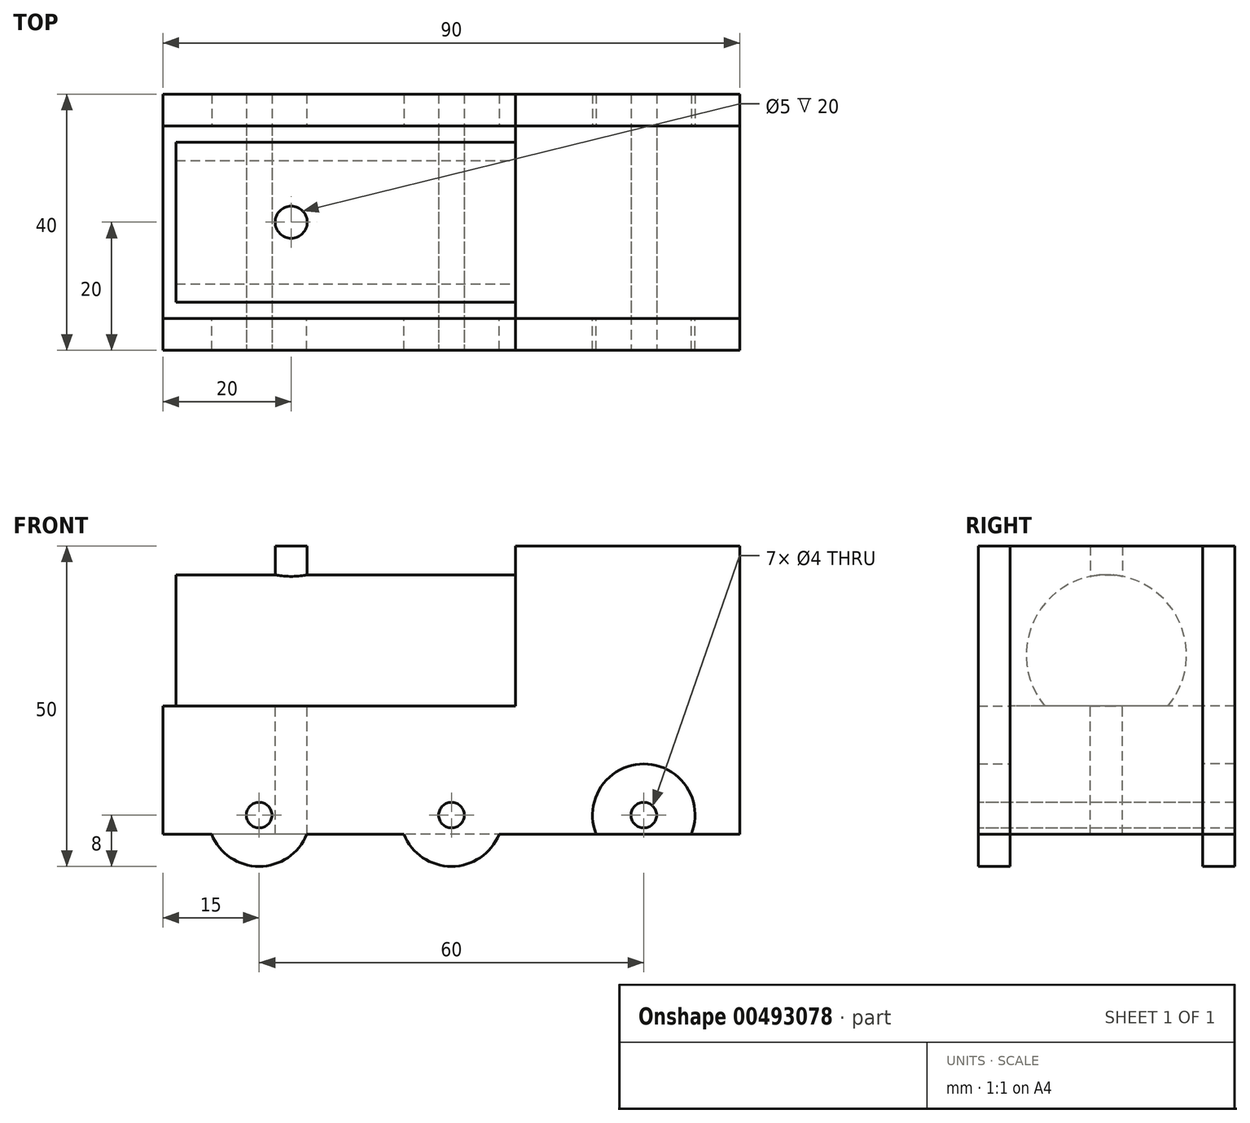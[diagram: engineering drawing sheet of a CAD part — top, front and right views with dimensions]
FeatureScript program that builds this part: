
annotation { "Feature Type Name" : "Feature", "Feature Type Description" : "" }
export const myFeature = defineFeature(function(context is Context, id is Id, definition is map)
    precondition{}
    {
        {
            var Q0;
            Q0=qCreatedBy(makeId("Top.planeOp"),FACE);
            var sketch = newSketch(context, id + "F0", { "sketchPlane" : qUnion([Q0])});
            skLineSegment(sketch, "E0.bottom", {"start": v(0, 0) * mm, "end": v(-90, 0) * mm});
            skLineSegment(sketch, "E0.top", {"start": v(0, -30) * mm, "end": v(-90, -30) * mm});
            skLineSegment(sketch, "E0.left", {"start": v(0, 0) * mm, "end": v(0, -30) * mm});
            skLineSegment(sketch, "E0.right", {"start": v(-90, 0) * mm, "end": v(-90, -30) * mm});
            skSolve(sketch);
        }
        {
            var Q0;
            Q0=makeQuery(id+"F0.imprint","IMPRINT",FACE,{"disambiguationData":[TD([[makeQuery(id+"F0.imprint","IMPRINT",EDGE,{"derivedFrom":sQuery(id+"F0.wireOp",EDGE,"E0.bottom")}),1.0]])]});
            extrude(context, id + "F1", {"entities" : qUnion([Q0]), "depth" : 20 * mm});
        }
        {
            var Q0;
            Q0=makeQuery(id+"F1.opExtrude","CAP_FACE",FACE,{"disambiguationData":[OSD([sQuery(id+"F0.wireOp",EDGE,"E0.bottom"),sQuery(id+"F0.wireOp",EDGE,"E0.top"),sQuery(id+"F0.wireOp",EDGE,"E0.left"),sQuery(id+"F0.wireOp",EDGE,"E0.right")])],"isStart":false});
            var sketch = newSketch(context, id + "F2", { "sketchPlane" : qUnion([Q0])});
            skLineSegment(sketch, "E1.bottom", {"start": v(0, 0) * mm, "end": v(-35, 0) * mm});
            skLineSegment(sketch, "E1.top", {"start": v(0, -30) * mm, "end": v(-35, -30) * mm});
            skLineSegment(sketch, "E1.left", {"start": v(0, 0) * mm, "end": v(0, -30) * mm});
            skLineSegment(sketch, "E1.right", {"start": v(-35, 0) * mm, "end": v(-35, -30) * mm});
            skSolve(sketch);
        }
        {
            var Q0;
            Q0 = qSketchRegion(id + "F2", true);
            extrude(context, id + "F3", {"entities" : qUnion([Q0]), "operationType" : NewBodyOperationType.ADD, "depth" : 25 * mm});
        }
        {
            var Q0;
            Q0=makeQuery(id+"F3.opExtrude","SWEPT_FACE",FACE,{"disambiguationData":[OSD([sQuery(id+"F2.wireOp",EDGE,"E1.right")])]});
            var sketch = newSketch(context, id + "F4", { "sketchPlane" : qUnion([Q0])});
            skArc(sketch, "E2", {"start": v(24.6, 20) * mm, "mid": v(15, 40.5) * mm, "end": v(5.4, 20) * mm});
            skPoint(sketch, "E2.centerSnap0", {"position": v(15, 20) * mm});
            skLineSegment(sketch, "E3", {"start": v(5.4, 20) * mm, "end": v(24.6, 20) * mm});
            skSolve(sketch);
        }
        {
            var Q0;
            Q0=makeQuery(id+"F4.imprint","IMPRINT",FACE,{"disambiguationData":[TD([[makeQuery(id+"F4.imprint","IMPRINT",EDGE,{"derivedFrom":sQuery(id+"F4.wireOp",EDGE,"E2")}),1.0]])]});
            extrude(context, id + "F5", {"entities" : qUnion([Q0]), "depth" : 53 * mm});
        }
        {
            var Q0;
            Q0=makeQuery(id+"F3.opExtrude","CAP_FACE",FACE,{"disambiguationData":[OSD([sQuery(id+"F2.wireOp",EDGE,"E1.bottom"),sQuery(id+"F2.wireOp",EDGE,"E1.top"),sQuery(id+"F2.wireOp",EDGE,"E1.left"),sQuery(id+"F2.wireOp",EDGE,"E1.right")])],"isStart":false});
            var sketch = newSketch(context, id + "F6", { "sketchPlane" : qUnion([Q0])});
            skLineSegment(sketch, "E4.0", {"start": v(-88, -27.5) * mm, "end": v(-88, -2.5) * mm});
            skLineSegment(sketch, "E5.0", {"start": v(-35, 0) * mm, "end": v(-35, -30) * mm});
            skLineSegment(sketch, "E6", {"start": v(-35, -15) * mm, "end": v(-88, -15) * mm, "construction": true});
            skCircle(sketch, "E7", {"center": v(-70, -15) * mm, "radius": 2.5 * mm});
            skSolve(sketch);
        }
        {
            var Q0;
            Q0=makeQuery(id+"F6.imprint","IMPRINT",FACE,{"disambiguationData":[TD([[makeQuery(id+"F6.imprint","IMPRINT",EDGE,{"derivedFrom":sQuery(id+"F6.wireOp",EDGE,"E7")}),1.0]])]});
            extrude(context, id + "F7", {"entities" : qUnion([Q0]), "operationType" : NewBodyOperationType.REMOVE, "oppositeDirection" : true, "depth" : 69.3 * mm});
        }
        {
            var Q0;
            Q0=makeQuery(id+"F1.opExtrude","CAP_FACE",FACE,{"disambiguationData":[OSD([sQuery(id+"F0.wireOp",EDGE,"E0.bottom"),sQuery(id+"F0.wireOp",EDGE,"E0.top"),sQuery(id+"F0.wireOp",EDGE,"E0.left"),sQuery(id+"F0.wireOp",EDGE,"E0.right")])],"isStart":false});
            var sketch = newSketch(context, id + "F8", { "sketchPlane" : qUnion([Q0])});
            skCircle(sketch, "E8.0", {"center": v(-70, -15) * mm, "radius": 2.5 * mm});
            skSolve(sketch);
        }
        {
            var Q0;
            Q0 = qSketchRegion(id + "F8", true);
            extrude(context, id + "F9", {"entities" : qUnion([Q0]), "operationType" : NewBodyOperationType.ADD, "depth" : 25 * mm});
        }
        {
            var Q0;
            Q0=makeQuery(id+"F3.boolean.opBoolean","MERGE",FACE,{"derivedFrom":[makeQuery(id+"F1.opExtrude","SWEPT_FACE",FACE,{"disambiguationData":[OSD([sQuery(id+"F0.wireOp",EDGE,"E0.top")])]}),makeQuery(id+"F3.opExtrude","SWEPT_FACE",FACE,{"disambiguationData":[OSD([sQuery(id+"F2.wireOp",EDGE,"E1.top")])]})]});
            var sketch = newSketch(context, id + "F10", { "sketchPlane" : qUnion([Q0])});
            skLineSegment(sketch, "E9", {"start": v(-90, 3) * mm, "end": v(0, 3) * mm, "construction": true});
            skCircle(sketch, "E10", {"center": v(-75, 3) * mm, "radius": 8 * mm});
            skCircle(sketch, "E11", {"center": v(-45, 3) * mm, "radius": 8 * mm});
            skCircle(sketch, "E12", {"center": v(-15, 3) * mm, "radius": 8 * mm});
            skSolve(sketch);
        }
        {
            var Q0;
            {var subQ0=sQuery(id+"F10.wireOp",EDGE,"E10");var subQ1=makeQuery(id+"F1.opExtrude","CAP_EDGE",EDGE,{"disambiguationData":[OSD([sQuery(id+"F0.wireOp",EDGE,"E0.top")])],"isStart":true});var subQ2=makeQuery(id+"F10.imprint","INTERSECT",VERTEX,{"disambiguationData":[OD(0.0)],"derivedFrom":[subQ1,subQ0]});Q0=makeQuery(id+"F10.imprint","IMPRINT",FACE,{"disambiguationData":[TD([[makeQuery(id+"F10.imprint","IMPRINT",EDGE,{"disambiguationData":[TD([[subQ2,1.0]])],"derivedFrom":subQ0}),1.0]])]});}
            var Q1;
            {var subQ0=sQuery(id+"F10.wireOp",EDGE,"E10");var subQ1=makeQuery(id+"F1.opExtrude","CAP_EDGE",EDGE,{"disambiguationData":[OSD([sQuery(id+"F0.wireOp",EDGE,"E0.top")])],"isStart":true});var subQ2=makeQuery(id+"F10.imprint","INTERSECT",VERTEX,{"disambiguationData":[OD(0.0)],"derivedFrom":[subQ1,subQ0]});Q1=makeQuery(id+"F10.imprint","IMPRINT",FACE,{"disambiguationData":[TD([[makeQuery(id+"F10.imprint","IMPRINT",EDGE,{"disambiguationData":[TD([[subQ2,-1.0]])],"derivedFrom":subQ0}),1.0]])]});}
            var Q2;
            {var subQ0=sQuery(id+"F10.wireOp",EDGE,"E11");var subQ1=makeQuery(id+"F1.opExtrude","CAP_EDGE",EDGE,{"disambiguationData":[OSD([sQuery(id+"F0.wireOp",EDGE,"E0.top")])],"isStart":true});var subQ2=makeQuery(id+"F10.imprint","INTERSECT",VERTEX,{"disambiguationData":[OD(0.0)],"derivedFrom":[subQ1,subQ0]});Q2=makeQuery(id+"F10.imprint","IMPRINT",FACE,{"disambiguationData":[TD([[makeQuery(id+"F10.imprint","IMPRINT",EDGE,{"disambiguationData":[TD([[subQ2,-1.0]])],"derivedFrom":subQ0}),1.0]])]});}
            var Q3;
            {var subQ0=sQuery(id+"F10.wireOp",EDGE,"E11");var subQ1=makeQuery(id+"F1.opExtrude","CAP_EDGE",EDGE,{"disambiguationData":[OSD([sQuery(id+"F0.wireOp",EDGE,"E0.top")])],"isStart":true});var subQ2=makeQuery(id+"F10.imprint","INTERSECT",VERTEX,{"disambiguationData":[OD(0.0)],"derivedFrom":[subQ1,subQ0]});Q3=makeQuery(id+"F10.imprint","IMPRINT",FACE,{"disambiguationData":[TD([[makeQuery(id+"F10.imprint","IMPRINT",EDGE,{"disambiguationData":[TD([[subQ2,1.0]])],"derivedFrom":subQ0}),1.0]])]});}
            var Q4;
            {var subQ0=sQuery(id+"F10.wireOp",EDGE,"E12");var subQ1=makeQuery(id+"F1.opExtrude","CAP_EDGE",EDGE,{"disambiguationData":[OSD([sQuery(id+"F0.wireOp",EDGE,"E0.top")])],"isStart":true});var subQ2=makeQuery(id+"F10.imprint","INTERSECT",VERTEX,{"disambiguationData":[OD(0.0)],"derivedFrom":[subQ1,subQ0]});Q4=makeQuery(id+"F10.imprint","IMPRINT",FACE,{"disambiguationData":[TD([[makeQuery(id+"F10.imprint","IMPRINT",EDGE,{"disambiguationData":[TD([[subQ2,1.0]])],"derivedFrom":subQ0}),-1.0]])]});}
            var Q5;
            {var subQ0=sQuery(id+"F10.wireOp",EDGE,"E12");var subQ1=makeQuery(id+"F1.opExtrude","CAP_EDGE",EDGE,{"disambiguationData":[OSD([sQuery(id+"F0.wireOp",EDGE,"E0.top")])],"isStart":true});var subQ2=makeQuery(id+"F10.imprint","INTERSECT",VERTEX,{"disambiguationData":[OD(0.0)],"derivedFrom":[subQ1,subQ0]});Q5=makeQuery(id+"F10.imprint","IMPRINT",FACE,{"disambiguationData":[TD([[makeQuery(id+"F10.imprint","IMPRINT",EDGE,{"disambiguationData":[TD([[subQ2,-1.0]])],"derivedFrom":subQ0}),-1.0]])]});}
            extrude(context, id + "F11", {"entities" : qUnion([Q0, Q1, Q2, Q3, Q4, Q5]), "depth" : 5 * mm});
        }
        {
            var Q0;
            Q0=qCreatedBy(makeId("Front.planeOp"),FACE);
            cPlane(context, id + "F12", {"entities" : qUnion([Q0]), "cplaneType" : CPlaneType.OFFSET, "offset" : 15 * mm, "width" : 150 * mm, "height" : 150 * mm});
        }
        {
            var Q0;
            Q0=makeQuery(id+"F11.opExtrude","SWEPT_BODY",BODY,{"disambiguationData":[OSD([sQuery(id+"F10.wireOp",EDGE,"E10")])]});
            var Q1;
            Q1=makeQuery(id+"F11.opExtrude","SWEPT_BODY",BODY,{"disambiguationData":[OSD([sQuery(id+"F10.wireOp",EDGE,"E11")])]});
            var Q2;
            Q2=makeQuery(id+"F11.opExtrude","SWEPT_BODY",BODY,{"disambiguationData":[OSD([sQuery(id+"F10.wireOp",EDGE,"E12")])]});
            var Q3;
            Q3=qCreatedBy(id+"F12.planeOp",FACE);
            mirror(context, id + "F13", {"entities" : qUnion([Q0, Q1, Q2]), "mirrorPlane" : qUnion([Q3])});
        }
        {
            var Q0;
            Q0=makeQuery(id+"F11.opExtrude","CAP_FACE",FACE,{"disambiguationData":[OSD([sQuery(id+"F10.wireOp",EDGE,"E10")])],"isStart":false});
            var sketch = newSketch(context, id + "F14", { "sketchPlane" : qUnion([Q0])});
            skCircle(sketch, "E13", {"center": v(-75, 3) * mm, "radius": 2 * mm});
            skCircle(sketch, "E14.0", {"center": v(-45, 3) * mm, "radius": 8 * mm});
            skCircle(sketch, "E15.0", {"center": v(-15, 3) * mm, "radius": 8 * mm});
            skCircle(sketch, "E16", {"center": v(-45, 3) * mm, "radius": 2 * mm});
            skCircle(sketch, "E17", {"center": v(-15, 3) * mm, "radius": 2 * mm});
            skSolve(sketch);
        }
        {
            var Q0;
            Q0=makeQuery(id+"F14.imprint","IMPRINT",FACE,{"disambiguationData":[TD([[makeQuery(id+"F14.imprint","IMPRINT",EDGE,{"derivedFrom":sQuery(id+"F14.wireOp",EDGE,"E16")}),1.0]])]});
            var Q1;
            Q1=makeQuery(id+"F14.imprint","IMPRINT",FACE,{"disambiguationData":[TD([[makeQuery(id+"F14.imprint","IMPRINT",EDGE,{"derivedFrom":sQuery(id+"F14.wireOp",EDGE,"E17")}),1.0]])]});
            var Q2;
            Q2=makeQuery(id+"F14.imprint","IMPRINT",FACE,{"disambiguationData":[TD([[makeQuery(id+"F14.imprint","IMPRINT",EDGE,{"derivedFrom":sQuery(id+"F14.wireOp",EDGE,"E13")}),1.0]])]});
            extrude(context, id + "F15", {"entities" : qUnion([Q0, Q1, Q2]), "operationType" : NewBodyOperationType.REMOVE, "oppositeDirection" : true, "depth" : 56.1 * mm});
        }
        {
            var Q0;
            Q0=makeQuery(id+"F11.opExtrude","CAP_FACE",FACE,{"disambiguationData":[OSD([sQuery(id+"F10.wireOp",EDGE,"E10")])],"isStart":false});
            var sketch = newSketch(context, id + "F16", { "sketchPlane" : qUnion([Q0])});
            skCircle(sketch, "E18.0", {"center": v(-75, 3) * mm, "radius": 2 * mm});
            skCircle(sketch, "E19.0", {"center": v(-45, 3) * mm, "radius": 2 * mm});
            skCircle(sketch, "E20.0", {"center": v(-15, 3) * mm, "radius": 2 * mm});
            skSolve(sketch);
        }
        {
            var Q0;
            Q0 = qSketchRegion(id + "F16", true);
            var Q1;
            Q1=makeQuery(id+"F13.opPattern","COPY",FACE,{"derivedFrom":makeQuery(id+"F11.opExtrude","CAP_FACE",FACE,{"disambiguationData":[OSD([sQuery(id+"F10.wireOp",EDGE,"E11")])],"isStart":false}),"instanceName":"1"});
            extrude(context, id + "F17", {"entities" : qUnion([Q0]), "endBound" : BoundingType.UP_TO_SURFACE, "oppositeDirection" : true, "endBoundEntityFace" : qUnion([Q1]), "depth" : 25 * mm});
        }
    });
